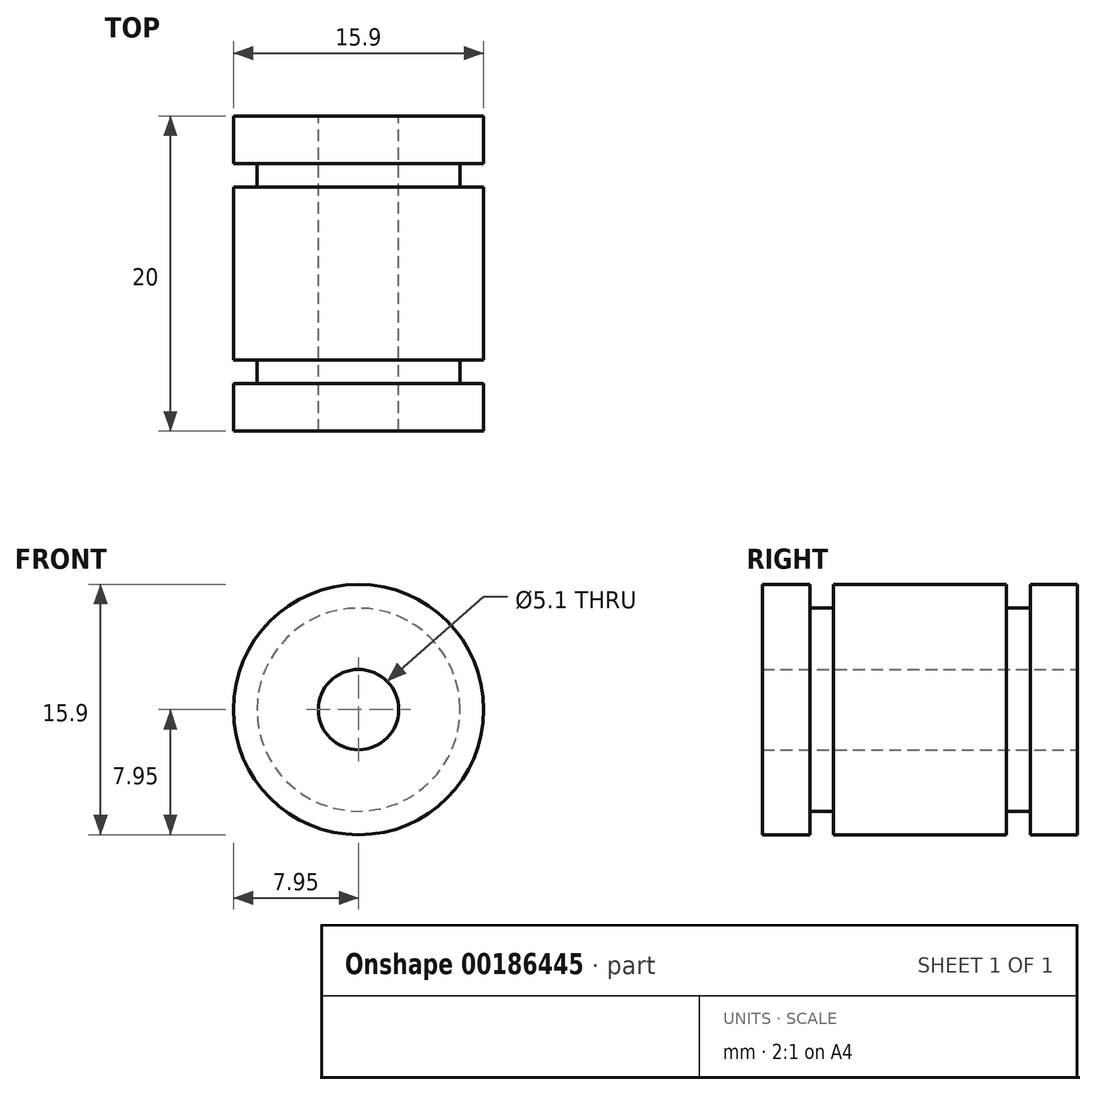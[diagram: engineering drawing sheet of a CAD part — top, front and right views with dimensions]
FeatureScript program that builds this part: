
annotation { "Feature Type Name" : "Feature", "Feature Type Description" : "" }
export const myFeature = defineFeature(function(context is Context, id is Id, definition is map)
    precondition{}
    {
        {
            var Q0;
            Q0=qCreatedBy(makeId("Right.planeOp"),FACE);
            var sketch = newSketch(context, id + "F0", { "sketchPlane" : qUnion([Q0])});
            skLineSegment(sketch, "E0", {"start": v(11.47, 0) * mm, "end": v(0, 0) * mm, "construction": true});
            skLineSegment(sketch, "E1", {"start": v(20, 2.55) * mm, "end": v(0, 2.55) * mm});
            skLineSegment(sketch, "E2", {"start": v(20, 2.55) * mm, "end": v(20, 4.95) * mm});
            skLineSegment(sketch, "E3", {"start": v(20, 4.95) * mm, "end": v(20, 4.95) * mm});
            skLineSegment(sketch, "E4", {"start": v(20, 4.95) * mm, "end": v(20, 7.95) * mm});
            skLineSegment(sketch, "E5", {"start": v(17, 7.95) * mm, "end": v(20, 7.95) * mm});
            skLineSegment(sketch, "E6", {"start": v(17, 7.95) * mm, "end": v(17, 6.45) * mm});
            skLineSegment(sketch, "E7", {"start": v(15.5, 6.45) * mm, "end": v(17, 6.45) * mm});
            skLineSegment(sketch, "E8", {"start": v(3, 6.45) * mm, "end": v(3, 7.95) * mm});
            skLineSegment(sketch, "E9", {"start": v(0, 7.95) * mm, "end": v(3, 7.95) * mm});
            skLineSegment(sketch, "E10", {"start": v(0, 7.95) * mm, "end": v(0, 2.55) * mm});
            skLineSegment(sketch, "E11", {"start": v(4.5, 6.45) * mm, "end": v(4.5, 7.95) * mm});
            skLineSegment(sketch, "E12", {"start": v(4.5, 7.95) * mm, "end": v(15.5, 7.95) * mm});
            skLineSegment(sketch, "E13", {"start": v(15.5, 7.95) * mm, "end": v(15.5, 6.45) * mm});
            skLineSegment(sketch, "E14.trimOffspring", {"start": v(4.5, 6.45) * mm, "end": v(3, 6.45) * mm});
            skSolve(sketch);
        }
        {
            var Q0;
            Q0=makeQuery(id+"F0.imprint","IMPRINT",FACE,{"disambiguationData":[TD([[makeQuery(id+"F0.imprint","IMPRINT",EDGE,{"derivedFrom":sQuery(id+"F0.wireOp",EDGE,"E1")}),-1.0]])]});
            var Q1;
            Q1=sQuery(id+"F0.wireOp",EDGE,"E0");
            revolve(context, id + "F1", {"entities" : qUnion([Q0]), "axis" : qUnion([Q1]), "revolveType" : RevolveType.FULL});
        }
    });
